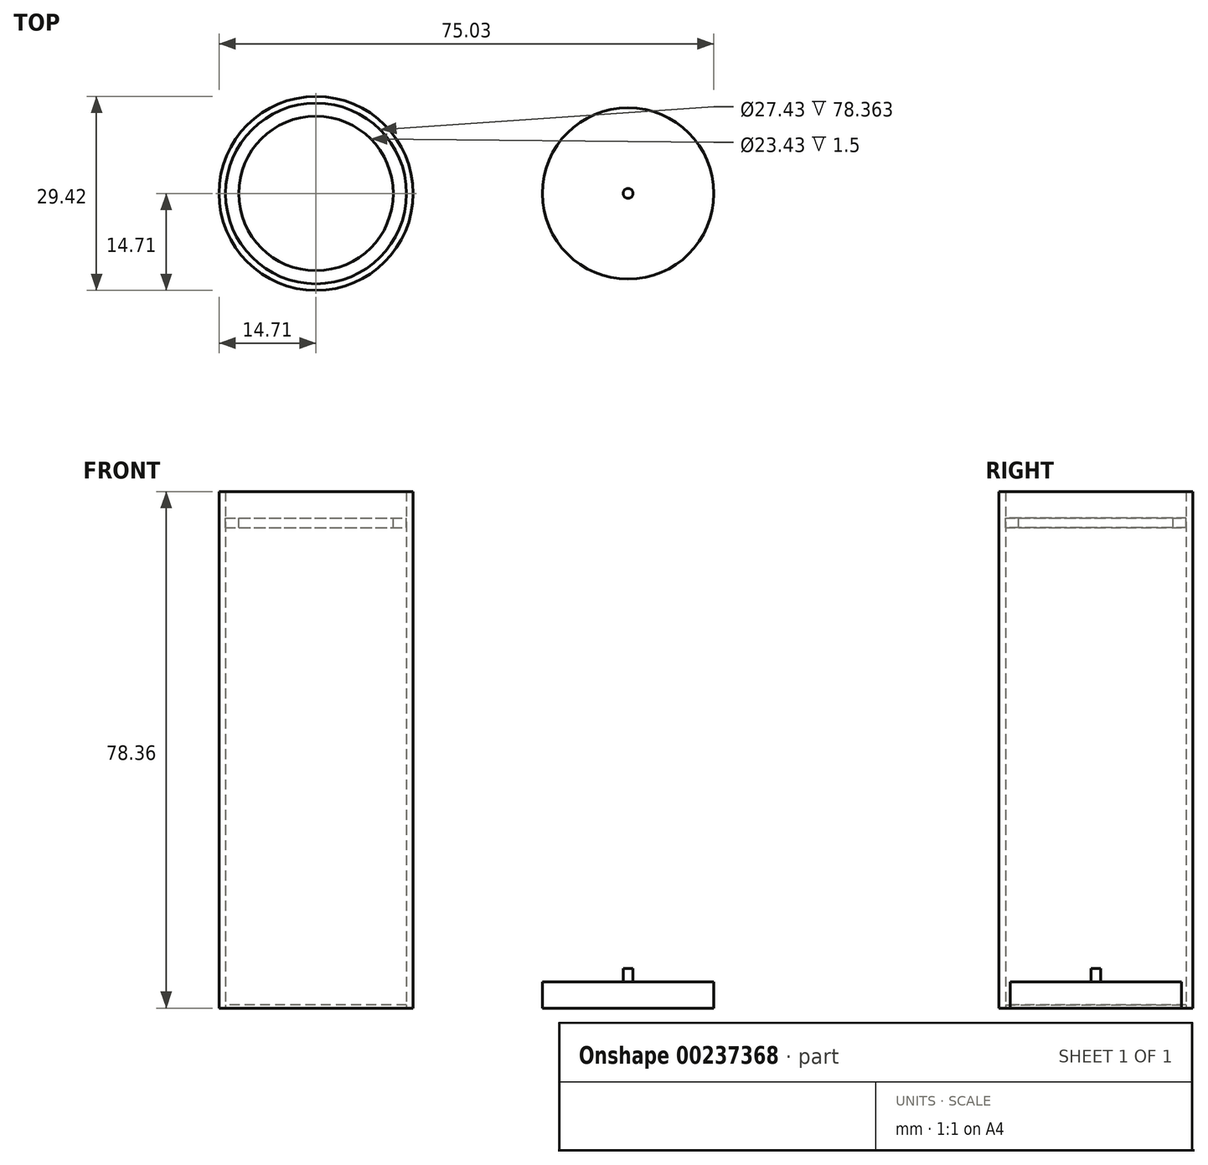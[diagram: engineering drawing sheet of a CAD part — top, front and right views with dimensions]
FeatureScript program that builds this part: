
annotation { "Feature Type Name" : "Feature", "Feature Type Description" : "" }
export const myFeature = defineFeature(function(context is Context, id is Id, definition is map)
    precondition{}
    {
        {
            var Q0;
            Q0=qCreatedBy(makeId("Top.planeOp"),FACE);
            var sketch = newSketch(context, id + "F0", { "sketchPlane" : qUnion([Q0])});
            skCircle(sketch, "E0", {"center": v(0, 0) * mm, "radius": 14.71 * mm});
            skCircle(sketch, "E1", {"center": v(0, 0) * mm, "radius": 13.71 * mm});
            skPoint(sketch, "E2", {"position": v(47.32, 0) * mm});
            skCircle(sketch, "E3", {"center": v(47.32, 0) * mm, "radius": 13 * mm});
            skPoint(sketch, "E4", {"position": v(47.32, 4.66) * mm});
            skSolve(sketch);
        }
        {
            var Q0;
            Q0=makeQuery(id+"F0.imprint","IMPRINT",FACE,{"disambiguationData":[TD([[makeQuery(id+"F0.imprint","IMPRINT",EDGE,{"derivedFrom":sQuery(id+"F0.wireOp",EDGE,"E1")}),1.0]])]});
            extrude(context, id + "F1", {"entities" : qUnion([Q0]), "depth" : 0.5 * mm, "offsetDistance" : 25 * mm});
        }
        {
            var Q0;
            Q0=makeQuery(id+"F0.imprint","IMPRINT",FACE,{"disambiguationData":[TD([[makeQuery(id+"F0.imprint","IMPRINT",EDGE,{"derivedFrom":sQuery(id+"F0.wireOp",EDGE,"E0")}),1.0]])]});
            extrude(context, id + "F2", {"entities" : qUnion([Q0]), "depth" : 78.36 * mm, "offsetDistance" : 25 * mm});
        }
        {
            var Q0;
            Q0=qCreatedBy(makeId("Front.planeOp"),FACE);
            var sketch = newSketch(context, id + "F3", { "sketchPlane" : qUnion([Q0])});
            skPoint(sketch, "E5", {"position": v(0, 74.36) * mm});
            skPoint(sketch, "E6", {"position": v(11.35, 0) * mm});
            skPoint(sketch, "E7", {"position": v(11.35, 74.36) * mm});
            skPoint(sketch, "E8", {"position": v(47.32, 0) * mm});
            skPoint(sketch, "E9", {"position": v(47.32, 4) * mm});
            skPoint(sketch, "E10", {"position": v(45.4, 0) * mm});
            skPoint(sketch, "E11", {"position": v(45.4, 4) * mm});
            skSolve(sketch);
        }
        {
            var Q0;
            Q0=qCreatedBy(makeId("Right.planeOp"),FACE);
            var sketch = newSketch(context, id + "F4", { "sketchPlane" : qUnion([Q0])});
            skPoint(sketch, "E12", {"position": v(12.83, 0) * mm});
            skPoint(sketch, "E13", {"position": v(12.83, 74.36) * mm});
            skPoint(sketch, "E14", {"position": v(4.66, 0) * mm});
            skPoint(sketch, "E15", {"position": v(4.66, 6.92) * mm});
            skSolve(sketch);
        }
        {
            var Q0;
            Q0=sQuery(id+"F4.wireOp",VERTEX,"E13");
            var Q1;
            Q1=sQuery(id+"F3.wireOp",VERTEX,"E5");
            var Q2;
            Q2=sQuery(id+"F3.wireOp",VERTEX,"E7");
            cPlane(context, id + "F5", {"entities" : qUnion([Q0, Q1, Q2]), "cplaneType" : CPlaneType.THREE_POINT, "offset" : 25 * mm, "width" : 150 * mm, "height" : 150 * mm});
        }
        {
            var Q0;
            Q0=qCreatedBy(id+"F5.planeOp",FACE);
            var sketch = newSketch(context, id + "F6", { "sketchPlane" : qUnion([Q0])});
            skCircle(sketch, "E16", {"center": v(0, 0) * mm, "radius": 13.71 * mm});
            skCircle(sketch, "E17", {"center": v(0, 0) * mm, "radius": 11.71 * mm});
            skSolve(sketch);
        }
        {
            var Q0;
            Q0=makeQuery(id+"F6.imprint","IMPRINT",FACE,{"disambiguationData":[TD([[makeQuery(id+"F6.imprint","IMPRINT",EDGE,{"derivedFrom":sQuery(id+"F6.wireOp",EDGE,"E16")}),1.0]])]});
            extrude(context, id + "F7", {"entities" : qUnion([Q0]), "depth" : 1.5 * mm, "offsetDistance" : 25 * mm});
        }
        {
            var Q0;
            Q0=makeQuery(id+"F0.imprint","IMPRINT",FACE,{"disambiguationData":[TD([[makeQuery(id+"F0.imprint","IMPRINT",EDGE,{"derivedFrom":sQuery(id+"F0.wireOp",EDGE,"E3")}),1.0]])]});
            extrude(context, id + "F8", {"entities" : qUnion([Q0]), "depth" : 4 * mm, "offsetDistance" : 25 * mm});
        }
        {
            var Q0;
            Q0=sQuery(id+"F4.wireOp",VERTEX,"E14");
            var Q1;
            Q1=sQuery(id+"F4.wireOp",VERTEX,"E15");
            var Q2;
            Q2=sQuery(id+"F0.wireOp",VERTEX,"E4");
            cPlane(context, id + "F9", {"entities" : qUnion([Q0, Q1, Q2]), "cplaneType" : CPlaneType.THREE_POINT, "offset" : 25 * mm, "width" : 150 * mm, "height" : 150 * mm});
        }
        {
            var Q0;
            Q0=qCreatedBy(id+"F9.planeOp",FACE);
            var sketch = newSketch(context, id + "F10", { "sketchPlane" : qUnion([Q0])});
            skPoint(sketch, "E18", {"position": v(47.32, 0) * mm});
            skPoint(sketch, "E19", {"position": v(47.32, 4) * mm});
            skSolve(sketch);
        }
        {
            var Q0;
            Q0=sQuery(id+"F3.wireOp",VERTEX,"E9");
            var Q1;
            Q1=sQuery(id+"F3.wireOp",VERTEX,"E11");
            var Q2;
            Q2=sQuery(id+"F10.wireOp",VERTEX,"E19");
            cPlane(context, id + "F11", {"entities" : qUnion([Q0, Q1, Q2]), "cplaneType" : CPlaneType.THREE_POINT, "offset" : 25 * mm, "width" : 150 * mm, "height" : 150 * mm});
        }
        {
            var Q0;
            Q0=qCreatedBy(id+"F11.planeOp",FACE);
            var sketch = newSketch(context, id + "F12", { "sketchPlane" : qUnion([Q0])});
            skPoint(sketch, "E20", {"position": v(47.32, 0) * mm});
            skCircle(sketch, "E21", {"center": v(47.32, 0) * mm, "radius": 0.75 * mm});
            skSolve(sketch);
        }
        {
            var Q0;
            Q0=makeQuery(id+"F12.imprint","IMPRINT",FACE,{"disambiguationData":[TD([[makeQuery(id+"F12.imprint","IMPRINT",EDGE,{"derivedFrom":sQuery(id+"F12.wireOp",EDGE,"E21")}),1.0]])]});
            extrude(context, id + "F13", {"entities" : qUnion([Q0]), "operationType" : NewBodyOperationType.ADD, "depth" : 2 * mm, "offsetDistance" : 25 * mm});
        }
    });
